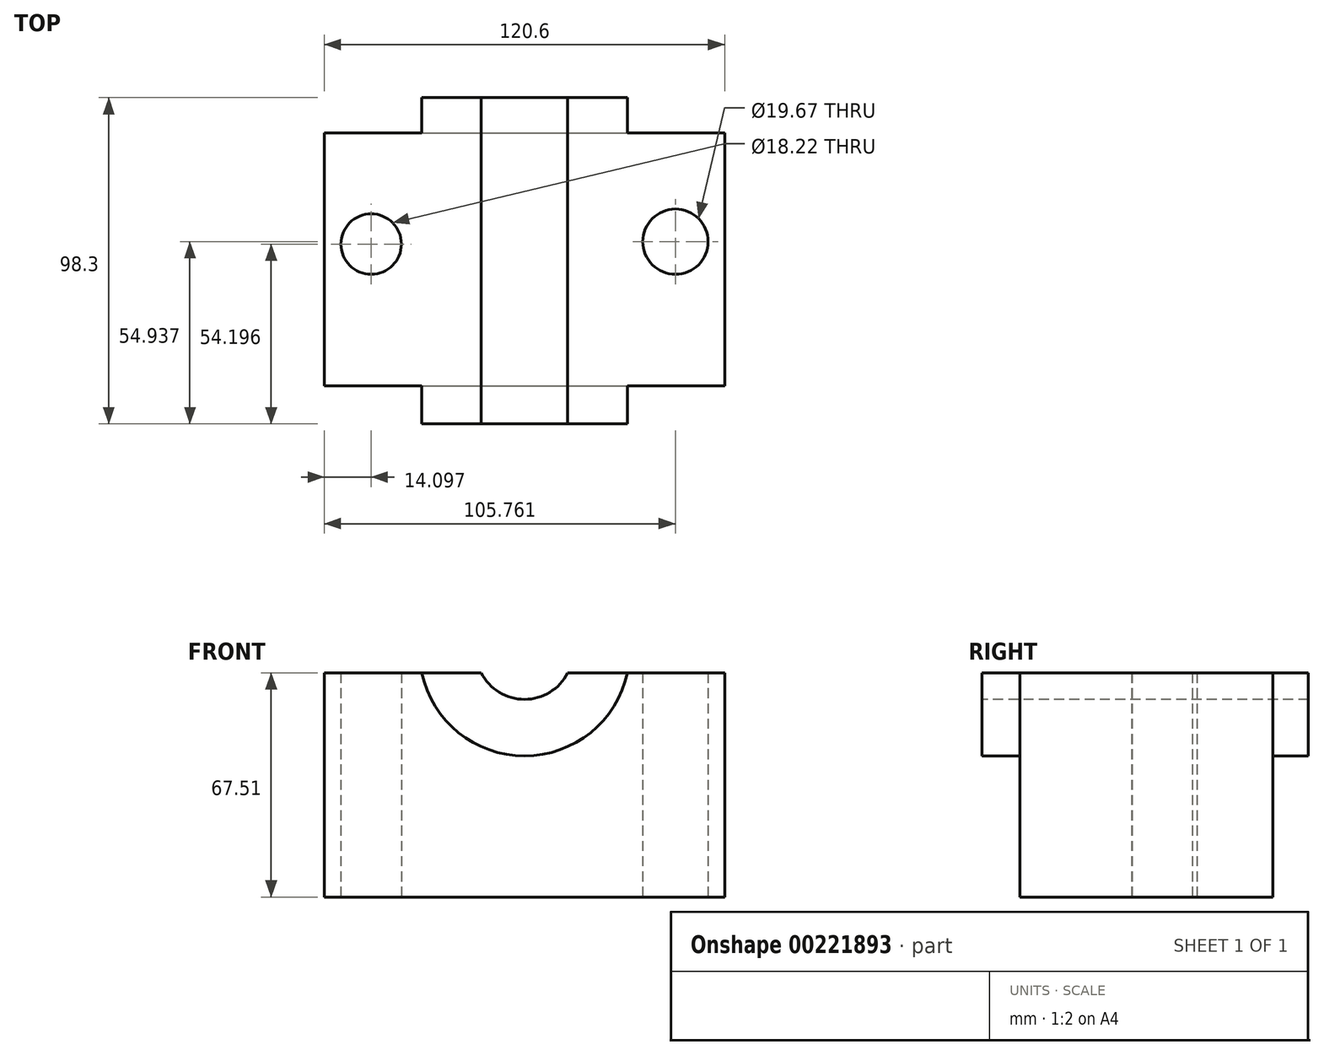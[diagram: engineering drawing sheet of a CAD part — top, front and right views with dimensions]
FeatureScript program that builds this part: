
annotation { "Feature Type Name" : "Feature", "Feature Type Description" : "" }
export const myFeature = defineFeature(function(context is Context, id is Id, definition is map)
    precondition{}
    {
        {
            var Q0;
            Q0=qCreatedBy(makeId("Front.planeOp"),FACE);
            var sketch = newSketch(context, id + "F0", { "sketchPlane" : qUnion([Q0])});
            skLineSegment(sketch, "E0.bottom", {"start": v(-60.3, 36.9) * mm, "end": v(60.3, 36.9) * mm});
            skLineSegment(sketch, "E0.top", {"start": v(-60.3, -36.9) * mm, "end": v(60.3, -36.9) * mm});
            skLineSegment(sketch, "E0.left", {"start": v(-60.3, 36.9) * mm, "end": v(-60.3, -36.9) * mm});
            skLineSegment(sketch, "E0.right", {"start": v(60.3, 36.9) * mm, "end": v(60.3, -36.9) * mm});
            skPoint(sketch, "E0.middle", {"position": v(0, 0) * mm});
            skSolve(sketch);
        }
        {
            var Q0;
            Q0 = qSketchRegion(id + "F0", true);
            extrude(context, id + "F1", {"entities" : qUnion([Q0]), "oppositeDirection" : true, "depth" : 76.2 * mm});
        }
        {
            var Q0;
            Q0=qCreatedBy(makeId("Front.planeOp"),FACE);
            var sketch = newSketch(context, id + "F2", { "sketchPlane" : qUnion([Q0])});
            skCircle(sketch, "E1", {"center": v(0, 37.3) * mm, "radius": 31.68 * mm});
            skSolve(sketch);
        }
        {
            var Q0;
            Q0 = qSketchRegion(id + "F2", true);
            extrude(context, id + "F3", {"entities" : qUnion([Q0]), "operationType" : NewBodyOperationType.ADD, "oppositeDirection" : true, "depth" : 86.87 * mm, "hasSecondDirection" : true, "secondDirectionOppositeDirection" : false, "secondDirectionDepth" : 11.43 * mm});
        }
        {
            var Q0;
            Q0=qCreatedBy(makeId("Right.planeOp"),FACE);
            var sketch = newSketch(context, id + "F4", { "sketchPlane" : qUnion([Q0])});
            skLineSegment(sketch, "E2.bottom", {"start": v(101.14, 30.6) * mm, "end": v(-18, 30.6) * mm});
            skLineSegment(sketch, "E2.top", {"start": v(101.14, 70.78) * mm, "end": v(-18, 70.78) * mm});
            skLineSegment(sketch, "E2.left", {"start": v(101.14, 30.6) * mm, "end": v(101.14, 70.78) * mm});
            skLineSegment(sketch, "E2.right", {"start": v(-18, 30.6) * mm, "end": v(-18, 70.78) * mm});
            skSolve(sketch);
        }
        {
            var Q0;
            Q0 = qSketchRegion(id + "F4", true);
            extrude(context, id + "F5", {"entities" : qUnion([Q0]), "operationType" : NewBodyOperationType.REMOVE, "endBound" : BoundingType.THROUGH_ALL, "oppositeDirection" : true, "depth" : 25.4 * mm, "hasSecondDirection" : true, "secondDirectionBound" : SecondDirectionBoundingType.THROUGH_ALL, "secondDirectionOppositeDirection" : false, "secondDirectionDepth" : 25.4 * mm});
        }
        {
            var Q0;
            Q0=qCreatedBy(makeId("Front.planeOp"),FACE);
            var sketch = newSketch(context, id + "F6", { "sketchPlane" : qUnion([Q0])});
            skCircle(sketch, "E3", {"center": v(0, 37.3) * mm, "radius": 14.64 * mm});
            skSolve(sketch);
        }
        {
            var Q0;
            Q0 = qSketchRegion(id + "F6", true);
            extrude(context, id + "F7", {"entities" : qUnion([Q0]), "operationType" : NewBodyOperationType.REMOVE, "endBound" : BoundingType.THROUGH_ALL, "oppositeDirection" : true, "depth" : 76.2 * mm, "hasSecondDirection" : true, "secondDirectionOppositeDirection" : false, "secondDirectionDepth" : 25.4 * mm});
        }
        {
            var Q0;
            Q0=qCreatedBy(makeId("Top.planeOp"),FACE);
            var sketch = newSketch(context, id + "F8", { "sketchPlane" : qUnion([Q0])});
            skCircle(sketch, "E4", {"center": v(-46.2, 42.77) * mm, "radius": 9.11 * mm});
            skCircle(sketch, "E5", {"center": v(45.46, 43.5) * mm, "radius": 9.84 * mm});
            skSolve(sketch);
        }
        {
            var Q0;
            Q0 = qSketchRegion(id + "F8", true);
            extrude(context, id + "F9", {"entities" : qUnion([Q0]), "operationType" : NewBodyOperationType.REMOVE, "endBound" : BoundingType.THROUGH_ALL, "depth" : 127 * mm, "hasSecondDirection" : true, "secondDirectionBound" : SecondDirectionBoundingType.THROUGH_ALL, "secondDirectionOppositeDirection" : true, "secondDirectionDepth" : 25.4 * mm});
        }
    });
